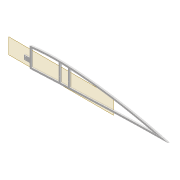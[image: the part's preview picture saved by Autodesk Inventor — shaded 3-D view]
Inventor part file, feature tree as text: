
AUTODESK INVENTOR PART (.ipt)
format: ipt  version: 2022 (Build 260153000, 153)  size: 409,088 bytes
history: native  units: mm
features: extrude x8, sketch x7, projected_geometry x6, fillet x2, shell x1, plane x1
ambient origin geometry x8: Origin, YZ Plane, XZ Plane, XY Plane, X Axis, Y Axis, Z Axis, Center Point
bodies: Solid1 (feature_tree)
feature tree (25):
  extrude  "Extrusion1"  Depth=5.0mm
  shell  "Shell1"  Thickness=2.0mm
  extrude  "Extrusion8"  Depth=5.9mm
  extrude  "Extrusion3"  Depth=10.0mm TaperAngle=0.0deg
  extrude  "Extrusion4"  Depth=2.0mm
  fillet  "Fillet1"  Radius=5.0mm
  sketch  "Sketch10"  dims[d22=4.0mm d23=0.0mm d31=2.0mm d32=5.0mm]
  extrude  "Extrusion5"  Depth=2.5mm
  plane  "Work Plane2"
  extrude  "Extrusion9"  Depth=1.6mm
  fillet  "Fillet2"  Radius=2.5mm
  extrude  "Extrusion10"  Depth=0.5mm
  extrude  "Extrusion11"  Depth=0.5mm TaperAngle=0.0deg
  sketch  "Sketch3"  dims[d0=4.0mm d1=0.0mm d2=5.0mm d7=2.0mm]
  sketch  "Sketch8"  dims[d8=2.0mm d9=5.9mm]
  sketch  "Sketch9"  dims[d13=10.0mm d14=0.0mm d16=10.0mm d17=0.0mm]
  projected_geometry  "Projected Loop4"
  projected_geometry  "Projected Loop10"
  sketch  "Sketch24"  dims[d34=1.6mm d35=2.5mm]
  projected_geometry  "Projected Loop11"
  projected_geometry  "Projected Loop12"
  projected_geometry  "Projected Loop13"
  sketch  "Sketch26"  dims[d37=5.0mm d38=1.6mm d40=2.5mm]
  projected_geometry  "Projected Loop14"
  sketch  "Sketch27"  dims[d62=80.0mm d63=6.0mm d64=4.0mm d65=0.0mm d66=3.0mm d67=12.0mm d68=5.0mm d69=15.0mm d70=12.0mm d71=3.05mm d72=10.0mm d73=0.0mm d74=2.0mm d75=90.0mm d76=20.0mm d77=0.5mm d78=10.0mm d79=0.0mm d80=10.0mm d81=0.0mm]
